# Revit family: 61e952f6-6e9b-4c1d-9296-4e66b2b940d9
name_source: partatom
category: Pipe Fittings
revit_build: Autodesk Revit 2016 (Build: 20161004_0715(x64)
units: mm (PartAtom-declared; Revit-internal decimal feet)

## family parameters
Always vertical = Yes
Cut with Voids When Loaded = No
OmniClass Number = 23.60.30.11.14
OmniClass Title = Pipework Fittings
Part Type = Tee
Round Connector Dimension = Use Radius
Shared = No
Work Plane-Based = No

## types (1)
- Standard
    04 CSI = 22 00 00
    95 CSI = 15100
    Assembly Code = D2090800
    CADworks URL = http://www.CADworks.net
    Compression Liner Material = Rubber - Schott
    Coupling Band Material = Steel - Schott - Stainless
    Description = Double Quarter Bend
    K Coefficient Table = Regular 45, 90 and 180 Elbow
    Lookup Table Name = Double_Quarter_Bend-Schott-Kimax-6519
    Loss Method = K Coefficient from Table
    Manufacturer = SCHOTT
    Model = 6519-1500, 6519-2015, 6519-2020, 6519-3000, 6519-4000, 6519-6000
    Pipe Material = Glass - Schott - Borosilicate
    Product URL = http://www.us.schott.com
    Seal Ring Material = Teflon - Schott
    Series = Kimax
    Subcategory = Bend Fitting
    URL = http://www.us.schott.com

## geometry (parser evidence)
native form markers: Blend x9, Revolve x4, Sweep x6
no freeform markers — native parametric forms only
